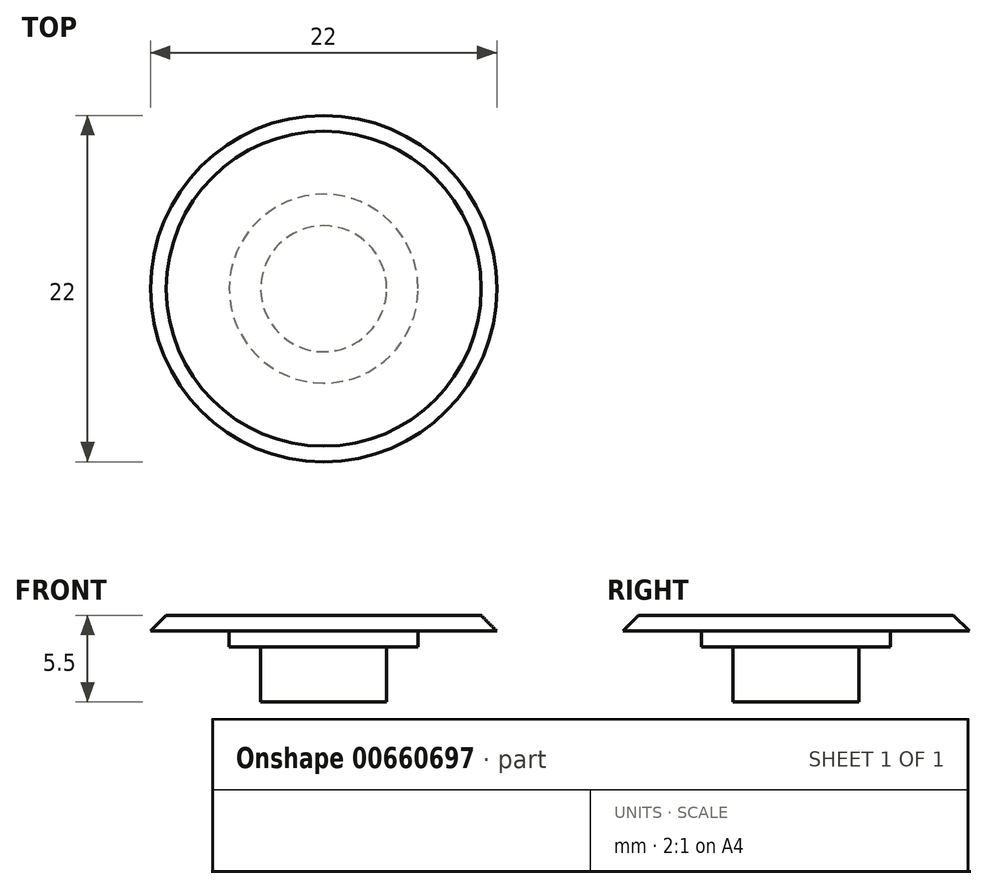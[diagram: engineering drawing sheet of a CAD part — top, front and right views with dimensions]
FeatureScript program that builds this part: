
annotation { "Feature Type Name" : "Feature", "Feature Type Description" : "" }
export const myFeature = defineFeature(function(context is Context, id is Id, definition is map)
    precondition{}
    {
        {
            var Q0;
            Q0=qCreatedBy(makeId("Top.planeOp"),FACE);
            var sketch = newSketch(context, id + "F0", { "sketchPlane" : qUnion([Q0])});
            skCircle(sketch, "E0", {"center": v(0, 0) * mm, "radius": 4 * mm});
            skSolve(sketch);
        }
        {
            var Q0;
            Q0=makeQuery(id+"F0.imprint","IMPRINT",FACE,{"disambiguationData":[TD([[makeQuery(id+"F0.imprint","IMPRINT",EDGE,{"derivedFrom":sQuery(id+"F0.wireOp",EDGE,"E0")}),1.0]])]});
            extrude(context, id + "F1", {"entities" : qUnion([Q0]), "depth" : 3.5 * mm, "offsetDistance" : 25 * mm});
        }
        {
            var Q0;
            Q0=makeQuery(id+"F1.opExtrude","CAP_FACE",FACE,{"disambiguationData":[OSD([sQuery(id+"F0.wireOp",EDGE,"E0")])],"isStart":false});
            var sketch = newSketch(context, id + "F2", { "sketchPlane" : qUnion([Q0])});
            skCircle(sketch, "E1", {"center": v(0, 0) * mm, "radius": 6 * mm});
            skSolve(sketch);
        }
        {
            var Q0;
            Q0 = qSketchRegion(id + "F2", true);
            extrude(context, id + "F3", {"entities" : qUnion([Q0]), "operationType" : NewBodyOperationType.ADD, "depth" : 1 * mm, "offsetDistance" : 25 * mm});
        }
        {
            var Q0;
            Q0=makeQuery(id+"F3.opExtrude","CAP_FACE",FACE,{"disambiguationData":[OSD([sQuery(id+"F2.wireOp",EDGE,"E1")])],"isStart":false});
            var sketch = newSketch(context, id + "F4", { "sketchPlane" : qUnion([Q0])});
            skCircle(sketch, "E2", {"center": v(0, 0) * mm, "radius": 11 * mm});
            skSolve(sketch);
        }
        {
            var Q0;
            Q0 = qSketchRegion(id + "F4", true);
            extrude(context, id + "F5", {"entities" : qUnion([Q0]), "operationType" : NewBodyOperationType.ADD, "depth" : 1 * mm, "offsetDistance" : 25 * mm});
        }
        {
            var Q0;
            Q0=makeQuery(id+"F5.opExtrude","CAP_FACE",FACE,{"disambiguationData":[OSD([sQuery(id+"F4.wireOp",EDGE,"E2")])],"isStart":false});
            var sketch = newSketch(context, id + "F6", { "sketchPlane" : qUnion([Q0])});
            skText(sketch, "E3", { "text": "MB", "fontName": "NotoSans-Bold.ttf"});
            const initialGuessF6  = {"E3": [-0.00892, -0.00365, 1, 0, 0.008]};
            skSetInitialGuess(sketch, initialGuessF6);
            skSolve(sketch);
        }
        {
            var Q0;
            Q0=makeQuery(id+"F5.opExtrude","CAP_EDGE",EDGE,{"disambiguationData":[OSD([sQuery(id+"F4.wireOp",EDGE,"E2")])],"isStart":false});
            chamfer(context, id + "F7", {"entities" : qUnion([Q0]), "width" : 1 * mm, "tangentPropagation" : true});
        }
    });
